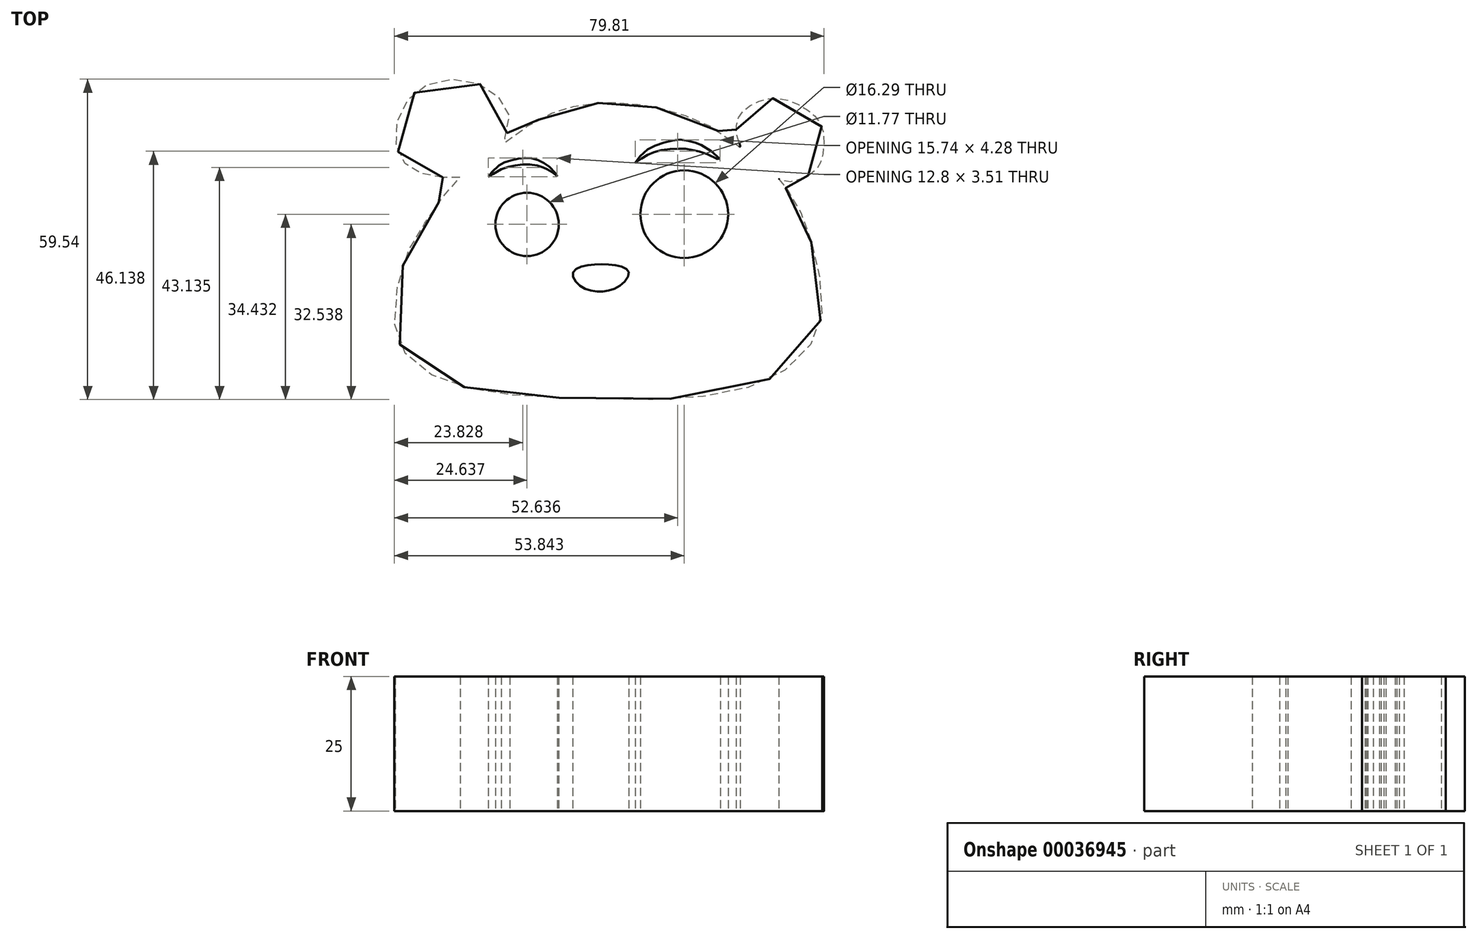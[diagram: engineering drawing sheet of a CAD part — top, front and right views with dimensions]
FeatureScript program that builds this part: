
annotation { "Feature Type Name" : "Feature", "Feature Type Description" : "" }
export const myFeature = defineFeature(function(context is Context, id is Id, definition is map)
    precondition{}
    {
        {
            var Q0;
            Q0=qCreatedBy(makeId("Top.planeOp"),FACE);
            var sketch = newSketch(context, id + "F0", { "sketchPlane" : qUnion([Q0])});
            skFitSpline(sketch, "E0", {"points": [v(-62.45, 31.86) * mm, v(-67.42, 33.02) * mm, v(-70.12, 35.33) * mm, v(-71.23, 40.38) * mm, v(-68.93, 46.33) * mm, v(-63.57, 49.75) * mm, v(-56.14, 49.45) * mm, v(-51.45, 46.03) * mm, v(-50.11, 41.13) * mm, v(-51.6, 38) * mm, v(-47.72, 40.7) * mm, v(-40.71, 44.38) * mm, v(-35.57, 45.5) * mm, v(-30.79, 45.81) * mm, v(-25.74, 45.4) * mm, v(-20, 44.2) * mm, v(-12.7, 41.37) * mm, v(-9.91, 39.38) * mm, v(-7.26, 37.56) * mm, v(-7.72, 39.35) * mm, v(-7.46, 43.12) * mm, v(-4.54, 45.64) * mm, v(0, 46.57) * mm, v(5.26, 44.45) * mm, v(8.11, 40.87) * mm, v(7.98, 35.44) * mm, v(6.44, 32.92) * mm, v(1.55, 31.07) * mm, v(0, 31.6) * mm, v(0.46, 30.87) * mm, v(1.95, 29.02) * mm, v(4.36, 24.68) * mm, v(6.7, 17.33) * mm, v(8.03, 7.65) * mm, v(5.36, 0) * mm, v(-3.15, -6.24) * mm, v(-18.26, -9.2) * mm, v(-37.25, -9.17) * mm, v(-51.4, -8.37) * mm, v(-63.41, -5.37) * mm, v(-69.97, 0) * mm, v(-71.38, 7.53) * mm, v(-68.88, 18.13) * mm, v(-65.08, 24.34) * mm, v(-60.74, 30.35) * mm, v(-59.19, 32.05) * mm, v(-62.45, 31.86) * mm]});
            skCircle(sketch, "E1", {"center": v(-46.8, 23.14) * mm, "radius": 5.89 * mm});
            skCircle(sketch, "E2", {"center": v(-17.59, 25.03) * mm, "radius": 8.15 * mm});
            skFitSpline(sketch, "E3", {"points": [v(-54, 31.98) * mm, v(-52.42, 33.71) * mm, v(-50.87, 34.72) * mm, v(-48.87, 35.28) * mm, v(-46.97, 35.51) * mm, v(-45.29, 35.26) * mm, v(-43.59, 34.5) * mm, v(-42.16, 33.36) * mm, v(-41.14, 32.13) * mm, v(-42.43, 33.06) * mm, v(-43.2, 33.47) * mm, v(-43.9, 33.78) * mm, v(-45.8, 34.24) * mm, v(-48, 34.24) * mm, v(-50, 33.92) * mm, v(-52.26, 33.03) * mm, v(-54, 31.98) * mm]});
            skFitSpline(sketch, "E4", {"points": [v(-26.66, 34.6) * mm, v(-25.28, 36.33) * mm, v(-23.53, 37.58) * mm, v(-21.3, 38.38) * mm, v(-19.28, 38.83) * mm, v(-17.59, 38.83) * mm, v(-15.85, 38.45) * mm, v(-15.15, 38.2) * mm, v(-12.36, 36.6) * mm, v(-10.9, 35.12) * mm, v(-12.78, 35.96) * mm, v(-14.89, 36.7) * mm, v(-16.12, 36.98) * mm, v(-17.59, 37.2) * mm, v(-18.9, 37.2) * mm, v(-21.15, 37.08) * mm, v(-22.84, 36.7) * mm, v(-24.21, 36.14) * mm, v(-25.3, 35.54) * mm, v(-26.66, 34.6) * mm]});
            skFitSpline(sketch, "E5", {"points": [v(-35.52, 15.54) * mm, v(-30.4, 15.54) * mm, v(-27.89, 14.3) * mm, v(-29.64, 11.67) * mm, v(-33.27, 10.67) * mm, v(-36.9, 11.67) * mm, v(-38.27, 14.17) * mm, v(-35.52, 15.54) * mm]});
            skSolve(sketch);
        }
        {
            var Q0;
            Q0=makeQuery(id+"F0.imprint","IMPRINT",FACE,{"disambiguationData":[TD([[makeQuery(id+"F0.imprint","IMPRINT",EDGE,{"derivedFrom":sQuery(id+"F0.wireOp",EDGE,"E0")}),-1.0]])]});
            extrude(context, id + "F1", {"entities" : qUnion([Q0]), "depth" : 25 * mm});
        }
    });
